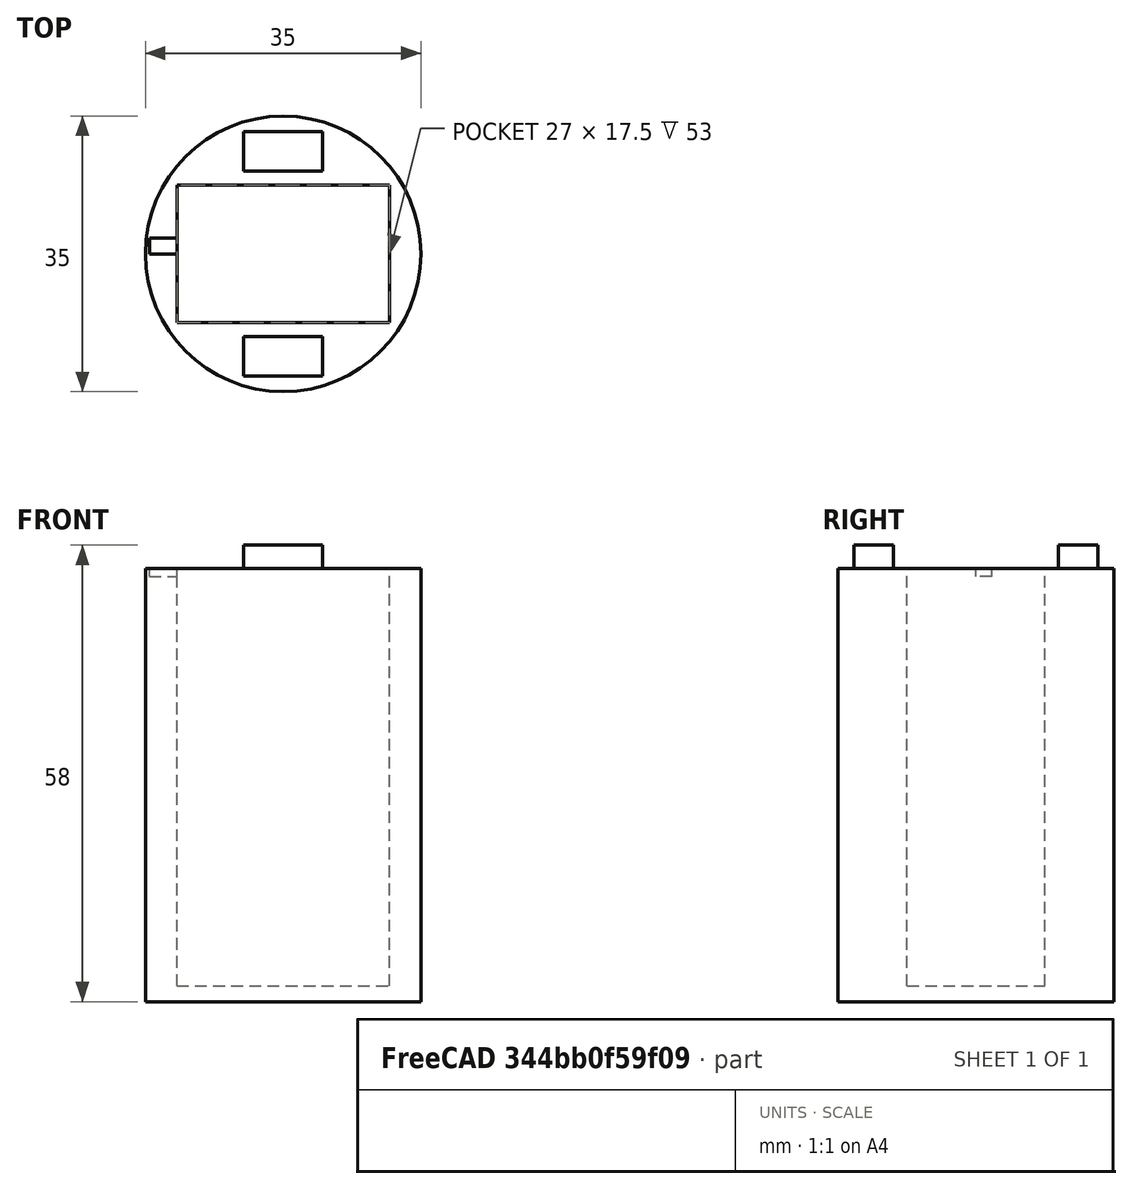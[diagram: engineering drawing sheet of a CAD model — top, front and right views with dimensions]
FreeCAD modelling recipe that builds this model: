
FCSTD DOCUMENT  (FreeCAD 0.14R3702 (Git))
Label: pied8
License: CC-BY 3.0
LicenseURL: http://creativecommons.org/licenses/by/3.0/
objects: Part::Box×4, Part::Cut×2, Part::Fuse×2, Part::Cylinder×1
note: 9 computed .brp shape members not serialized (recipe doc carries the construction recipe); baked Part::Feature solids carry a one-line shape summary decoded from their .brp

FEATURE [Part::Cylinder] Cylinder
  Angle = 360
  Height = 55
  Radius = 17.5
FEATURE [Part::Box] Box
  Height = 53
  Length = 27
  Placement = pos=(-13.5,-8.75,2) rot=(0,0,1;0rad)
  Width = 17.5
FEATURE [Part::Box] Box001
  Height = 3
  Length = 10
  Placement = pos=(-5,10.5,55) rot=(0,0,1;0rad)
  Width = 5
FEATURE [Part::Box] Box002
  Height = 3
  Length = 10
  Placement = pos=(-5,-15.5,55) rot=(0,0,1;0rad)
  Width = 5
FEATURE [Part::Cut] Cut
  Base = -> Cylinder
  Tool = -> Box
FEATURE [Part::Fuse] Fusion
  Base = -> Box001
  Tool = -> Cut
FEATURE [Part::Fuse] Fusion001
  Base = -> Box002
  Tool = -> Fusion
FEATURE [Part::Box] Box003
  Height = 2
  Length = 4
  Placement = pos=(-17,0,54) rot=(0,0,1;0rad)
  Width = 2
FEATURE [Part::Cut] Cut001
  Base = -> Fusion001
  Tool = -> Box003
